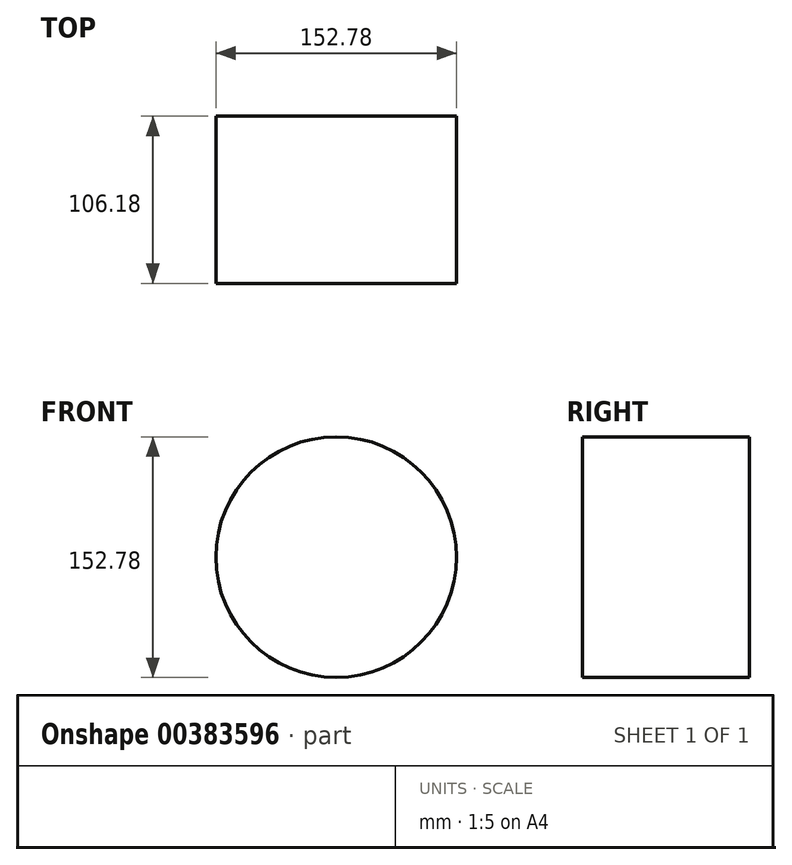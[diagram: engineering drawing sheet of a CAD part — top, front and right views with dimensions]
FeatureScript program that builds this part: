
annotation { "Feature Type Name" : "Feature", "Feature Type Description" : "" }
export const myFeature = defineFeature(function(context is Context, id is Id, definition is map)
    precondition{}
    {
        {
            var Q0;
            Q0=qCreatedBy(makeId("Front.planeOp"),FACE);
            var sketch = newSketch(context, id + "F0", { "sketchPlane" : qUnion([Q0])});
            skCircle(sketch, "E0", {"center": v(0, 0) * mm, "radius": 76.4 * mm});
            skSolve(sketch);
        }
        {
            var Q0;
            Q0=makeQuery(id+"F0.imprint","IMPRINT",FACE,{"disambiguationData":[TD([[makeQuery(id+"F0.imprint","IMPRINT",EDGE,{"derivedFrom":sQuery(id+"F0.wireOp",EDGE,"E0")}),1.0]])]});
            extrude(context, id + "F1", {"entities" : qUnion([Q0]), "endBound" : BoundingType.SYMMETRIC, "depth" : 106.17 * mm});
        }
    });
